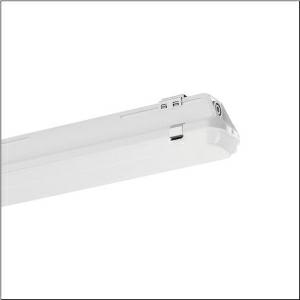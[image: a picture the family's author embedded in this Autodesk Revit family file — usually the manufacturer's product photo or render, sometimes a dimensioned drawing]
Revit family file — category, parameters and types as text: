
# Revit family: monsun_r__11_emergency_51fp10dp467l3h_32f3
name_source: partatom
category: Lighting Fixtures
units: mm (PartAtom-declared; Revit-internal decimal feet)

## family parameters
Cut with Voids When Loaded = No
Host = Face
Light Source = No
Part Type = Normal
Room Calculation Point = No
Round Connector Dimension = Use Diameter
Shared = No

## types (1)
- --- (1 x LED, 1010 lm, 6.2 W, 4000K)
    Apparent Load = 6 VA
    CIE Flux Codes = 47 77 93 94 100
    Color Rendering = 80
    Color Temperature = 4000K
    Default Elevation = 1800 mm
    Description = Monsun® 11 emergency, damp-proof luminaire, chain hanger, primary optical cover: enclosure, of PMMA, light emission: direct distribution, primary light characteristic: symmetric, installation type: suspended mounting, surface-mounted, horizontal mounting, vertical mounting, LED, rated luminous flux: 6.050lm, luminous efficacy: 192lm/W, light colour: 840, colour temperature: 4000K, control gear: DALI 2, with terminal, 5+3-pole, max. 2.5mm², mains connection: 220..240V, AC, 50/60Hz, rated input power: 35W, control gear: single battery element, battery: LiFePO4, 9Ah, luminaire housing, of glass-fibre reinforced polyester, uncoated, bright grey, incl. chain hanger, length: 1.590mm, width: 90mm, height: 88mm, clip for enclosure, of stainless steel (V2A), ceiling mounting element, of stainless steel (V2A), chain hanger, of stainless steel (V2A), protection rating (complete): IP66, insulation class (complete): insulation class I (protective earthing), certification: CE, UKCA, protection symbol: D, impact resistance: IK04, permissible operating ambient temperature: +5..+35°C, standard: EN 50419, EN 60598-2-1, EN 60598-2-22, corresponds to IFS (International Featured Standards) requirements for safety and quality in the food industry, for indoor or canopied outdoor use, no direct snow, no direct sun, no direct rain, LABS conformity tested according to VDMA 24364:2018-05, contact your sales advisor before using the luminaires in applications with unclear chemical exposure, large temperature fluctuations or condensation-forming humidity, packaging unit: 1 piece
    Height = 89 mm
    Lamp = 1 x LED
    Lamp Light Flux = 1010 lm
    Lamp Power = 6.2 W
    Lamp count = 1
    Length = 1590 mm
    Luminous efficacy = 163 lm/W
    Manufacturer = Siteco
    ModVariant = No
    Model = 51FP10DP467L3H
    Mounting Place = Ceiling
    Mounting Type = Surface mounted
    Number of Poles = 1
    OnlyDefault = Yes
    Power Factor = 1
    Product Name = Monsun® 11 emergency
    Product group = damp-proof luminaire
    ProductGroupID = 300
    Protection Class = Protection class I
    Protection Degree = IP 66
    RLX_Detail_Level = 1
    RLX_Emergency_Light_Flux = 0 lm
    RLX_Emergency_Type = 0
    RLX_Emergency_Type_DB = No
    RlxData = <blob elided: 92725 chars, md5=1821e0b8>
    Socket = socket
    Standby Power = 0 W
    System Light Flux = 1010 lm
    System Power = 6 W
    Type Comments = : emergency light operation: 3 h
    Type Image = l_1349237.jpg
    URL = http://relux.com
    VarID = @adj_017966
    Voltage = 0 V
    Weight = 0.00 kg
    Width = 90 mm

## geometry (parser evidence)
native form markers: Blend x4, Sweep x16
no freeform markers — native parametric forms only
